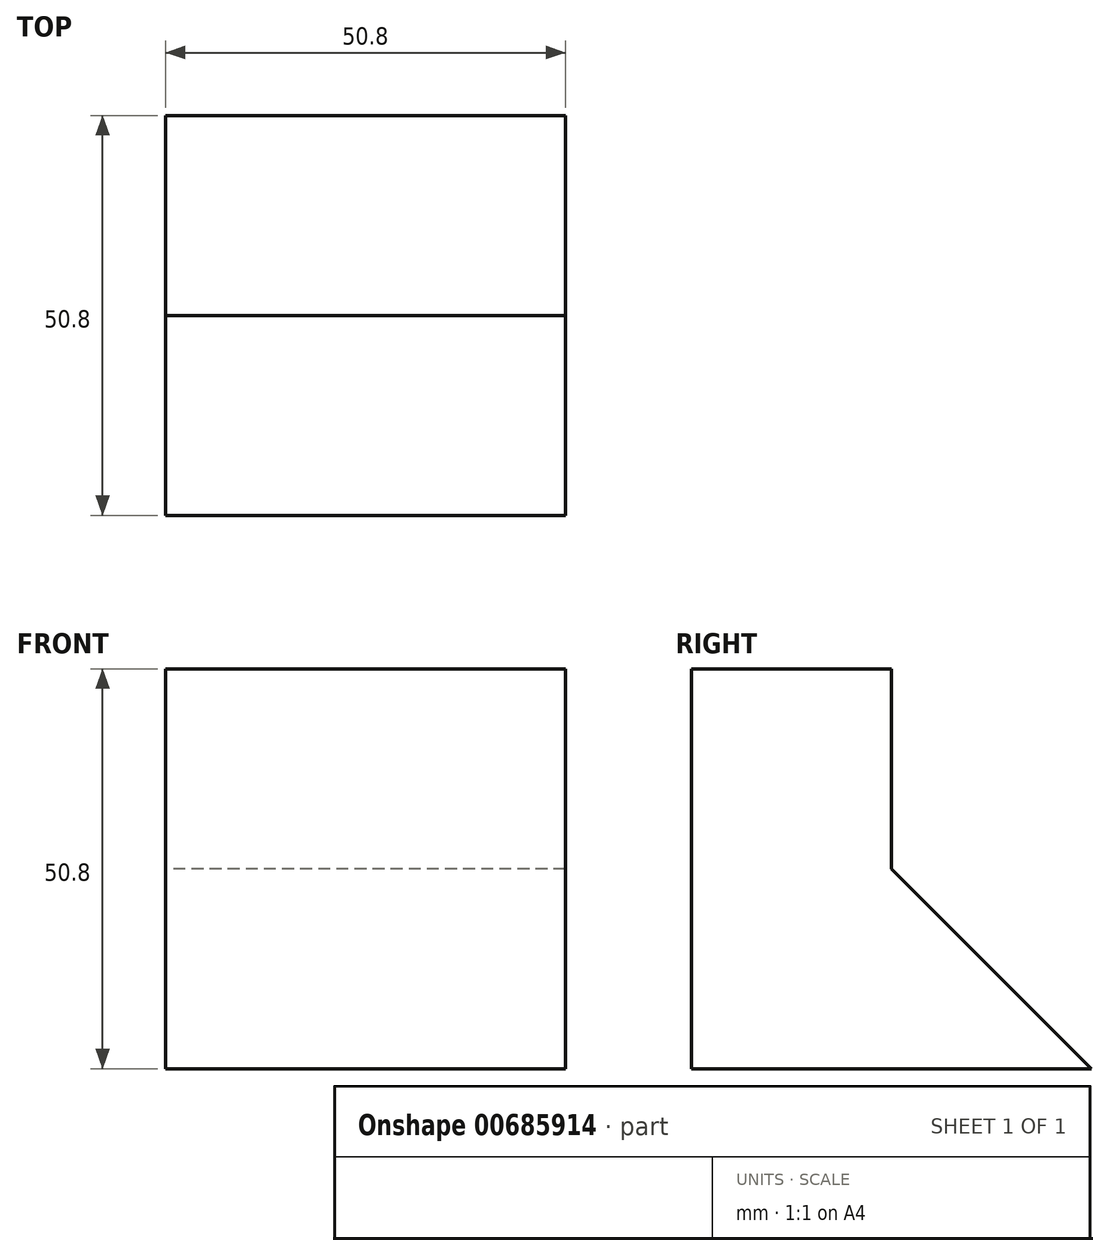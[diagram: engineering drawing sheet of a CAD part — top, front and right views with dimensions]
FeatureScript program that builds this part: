
annotation { "Feature Type Name" : "Feature", "Feature Type Description" : "" }
export const myFeature = defineFeature(function(context is Context, id is Id, definition is map)
    precondition{}
    {
        {
            var Q0;
            Q0=qCreatedBy(makeId("Right.planeOp"),FACE);
            var sketch = newSketch(context, id + "F0", { "sketchPlane" : qUnion([Q0])});
            skLineSegment(sketch, "E0", {"start": v(0, -39.81) * mm, "end": v(-50.8, -39.81) * mm});
            skLineSegment(sketch, "E1", {"start": v(-50.8, -39.81) * mm, "end": v(-50.8, 10.99) * mm});
            skLineSegment(sketch, "E2", {"start": v(-50.8, 10.99) * mm, "end": v(-25.4, 10.99) * mm});
            skLineSegment(sketch, "E3", {"start": v(-25.4, 10.99) * mm, "end": v(-25.4, -14.41) * mm});
            skLineSegment(sketch, "E4", {"start": v(-25.4, -14.41) * mm, "end": v(0, -39.81) * mm});
            skSolve(sketch);
        }
        {
            var Q0;
            Q0=makeQuery(id+"F0.imprint","IMPRINT",FACE,{"disambiguationData":[TD([[makeQuery(id+"F0.imprint","IMPRINT",EDGE,{"derivedFrom":sQuery(id+"F0.wireOp",EDGE,"E0")}),-1.0]])]});
            extrude(context, id + "F1", {"entities" : qUnion([Q0]), "depth" : 50.8 * mm, "offsetDistance" : 25.4 * mm});
        }
    });
